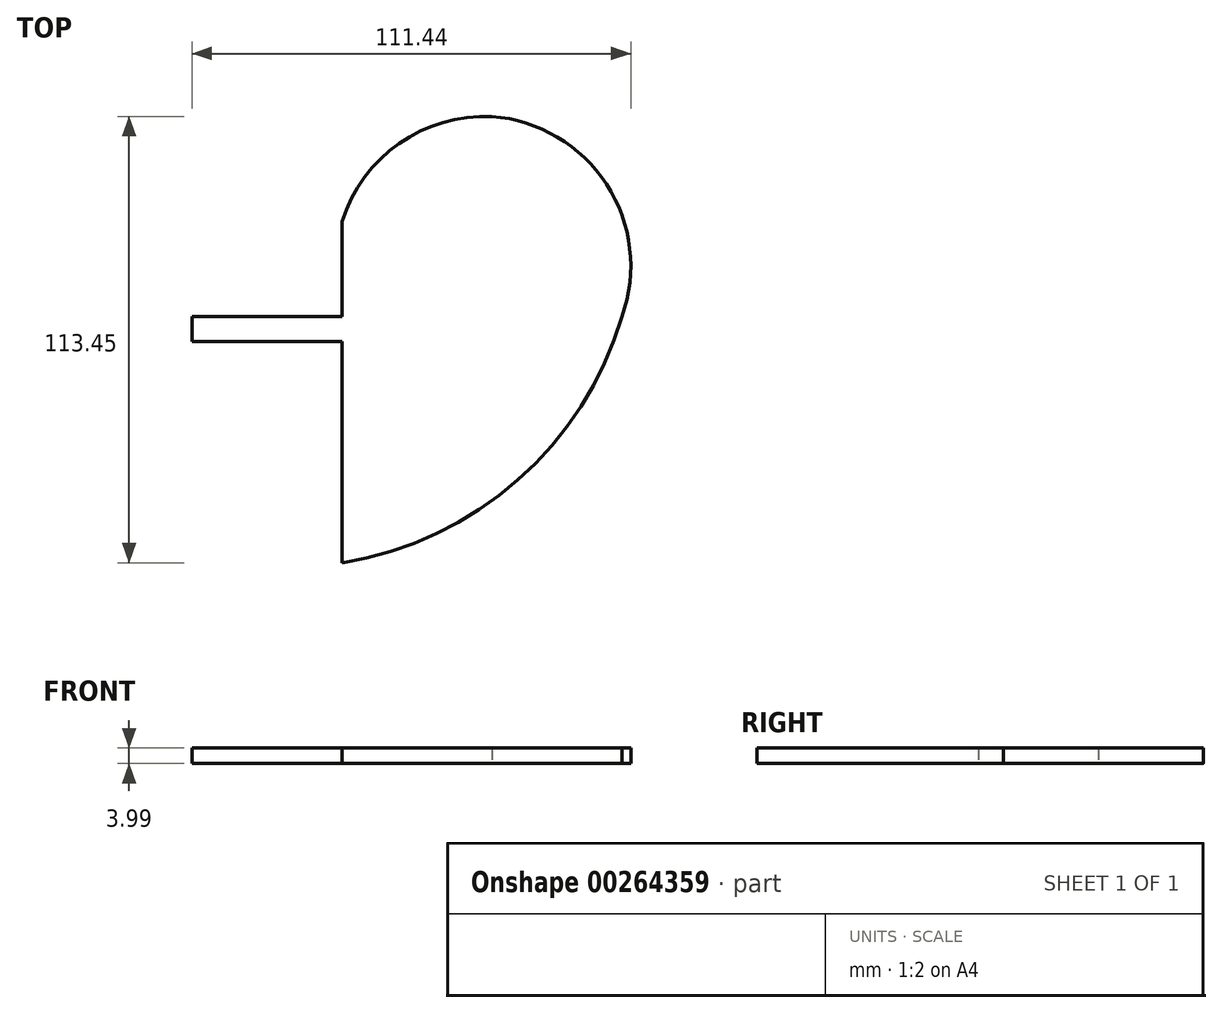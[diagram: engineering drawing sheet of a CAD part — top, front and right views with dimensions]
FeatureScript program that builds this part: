
annotation { "Feature Type Name" : "Feature", "Feature Type Description" : "" }
export const myFeature = defineFeature(function(context is Context, id is Id, definition is map)
    precondition{}
    {
        {
            var Q0;
            Q0=qCreatedBy(makeId("Top.planeOp"),FACE);
            var sketch = newSketch(context, id + "F0", { "sketchPlane" : qUnion([Q0])});
            skLineSegment(sketch, "E0", {"start": v(0, 0) * mm, "end": v(0, -56.26) * mm});
            skLineSegment(sketch, "E1", {"start": v(0, 6.35) * mm, "end": v(0, 30.48) * mm});
            skLineSegment(sketch, "E2", {"start": v(0, 6.35) * mm, "end": v(-38.1, 6.35) * mm});
            skLineSegment(sketch, "E3", {"start": v(-38.1, 6.35) * mm, "end": v(-38.1, 0) * mm});
            skLineSegment(sketch, "E4", {"start": v(-38.1, 0) * mm, "end": v(0, 0) * mm});
            skArc(sketch, "E5", {"start": v(38.1, 57.15) * mm, "mid": v(14.5, 50.3) * mm, "end": v(0, 30.48) * mm});
            skArc(sketch, "E6", {"start": v(71.12, 6.35) * mm, "mid": v(67.18, 39.92) * mm, "end": v(38.1, 57.15) * mm});
            skArc(sketch, "E7", {"start": v(0, -56.26) * mm, "mid": v(44.6, -35.22) * mm, "end": v(71.12, 6.35) * mm});
            skSolve(sketch);
        }
        {
            var Q0;
            Q0=makeQuery(id+"F0.imprint","IMPRINT",FACE,{"disambiguationData":[TD([[makeQuery(id+"F0.imprint","IMPRINT",EDGE,{"derivedFrom":sQuery(id+"F0.wireOp",EDGE,"E0")}),1.0]])]});
            extrude(context, id + "F1", {"entities" : qUnion([Q0]), "depth" : 4 * mm});
        }
    });
